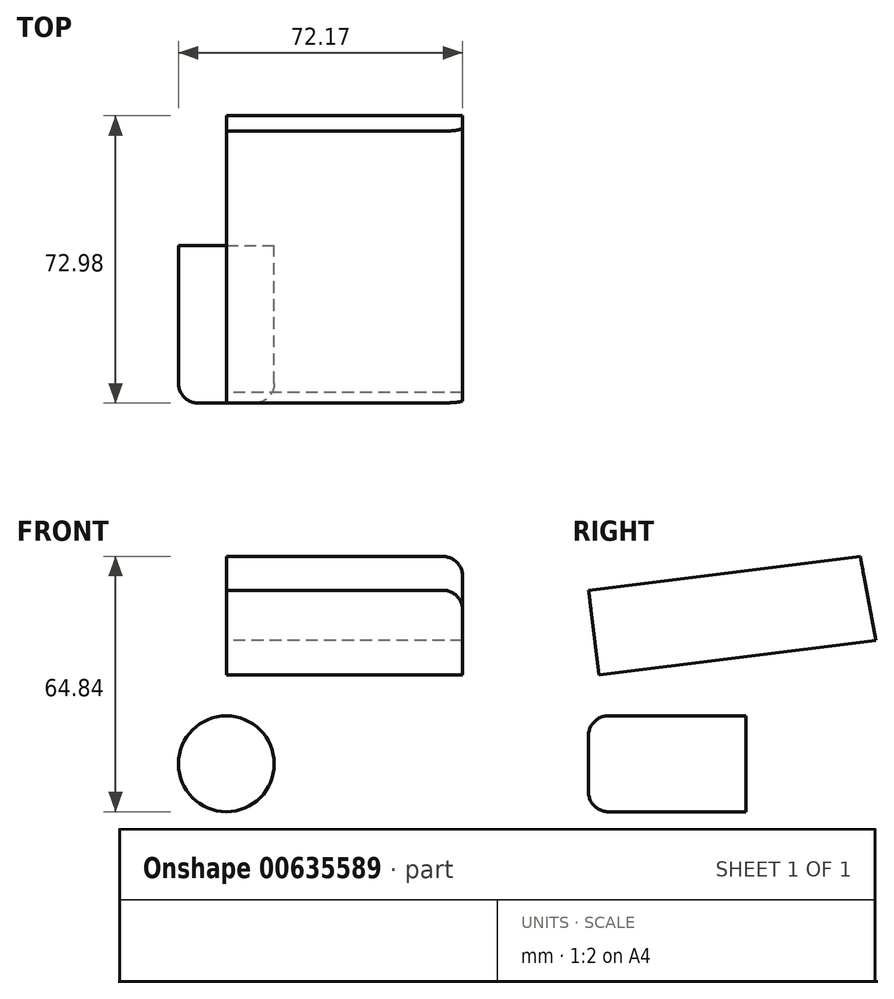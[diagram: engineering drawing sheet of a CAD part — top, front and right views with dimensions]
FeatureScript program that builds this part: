
annotation { "Feature Type Name" : "Feature", "Feature Type Description" : "" }
export const myFeature = defineFeature(function(context is Context, id is Id, definition is map)
    precondition{}
    {
        {
            var Q0;
            Q0=qCreatedBy(makeId("Front.planeOp"),FACE);
            var sketch = newSketch(context, id + "F0", { "sketchPlane" : qUnion([Q0])});
            skCircle(sketch, "E0", {"center": v(0, 0) * mm, "radius": 12.17 * mm});
            skSolve(sketch);
        }
        {
            var Q0;
            Q0 = qSketchRegion(id + "F0", true);
            extrude(context, id + "F1", {"entities" : qUnion([Q0]), "depth" : 40 * mm, "offsetDistance" : 25 * mm});
        }
        {
            var Q0;
            Q0=makeQuery(id+"F1.opExtrude","CAP_EDGE",EDGE,{"disambiguationData":[OSD([sQuery(id+"F0.wireOp",EDGE,"E0")])],"isStart":false});
            fillet(context, id + "F2", {"entities" : qUnion([Q0]), "radius" : 5 * mm, "tangentPropagation" : true, "allowEdgeOverflow" : false});
        }
        {
            var Q0;
            Q0=qCreatedBy(makeId("Right.planeOp"),FACE);
            var sketch = newSketch(context, id + "F3", { "sketchPlane" : qUnion([Q0])});
            skLineSegment(sketch, "E1", {"start": v(-39.98, 44.1) * mm, "end": v(29.05, 52.67) * mm});
            skLineSegment(sketch, "E2", {"start": v(-39.98, 44.1) * mm, "end": v(-37.31, 22.65) * mm});
            skLineSegment(sketch, "E3", {"start": v(-37.31, 22.65) * mm, "end": v(32.98, 31.38) * mm});
            skLineSegment(sketch, "E4", {"start": v(32.98, 31.38) * mm, "end": v(29.05, 52.67) * mm});
            skSolve(sketch);
        }
        {
            var Q0;
            Q0 = qSketchRegion(id + "F3", true);
            extrude(context, id + "F4", {"entities" : qUnion([Q0]), "depth" : 60 * mm, "offsetDistance" : 25 * mm});
        }
        {
            var Q0;
            Q0=makeQuery(id+"F4.opExtrude","CAP_EDGE",EDGE,{"disambiguationData":[OSD([sQuery(id+"F3.wireOp",EDGE,"E1")])],"isStart":false});
            fillet(context, id + "F5", {"entities" : qUnion([Q0]), "radius" : 5 * mm, "tangentPropagation" : true, "allowEdgeOverflow" : false});
        }
    });
